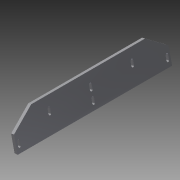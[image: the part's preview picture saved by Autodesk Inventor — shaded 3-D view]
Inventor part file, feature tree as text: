
AUTODESK INVENTOR PART (.ipt)
format: ipt  version: 2011 SP2 (Build 150309200, 309)  size: 1,105,920 bytes
history: native  units: mm
features: extrude x40, sketch x23, projected_geometry x14, fillet x12, mirror x2, pattern_linear x2, plane x1, chamfer x1, hole x1
ambient origin geometry x8: Origin, YZ Plane, XZ Plane, XY Plane, X Axis, Y Axis, Z Axis, Center Point
feature tree (96):
  sketch  "Sketch1"  dims[d0=200.0mm d1=200.0mm]
  extrude  "Extrusion3"  Depth=200.0mm
  extrude  "Extrusion4"  Depth=10.5mm
  extrude  "Extrusion5"  Depth=6.5mm
  extrude  "Extrusion6"  Depth=53.3mm
  extrude  "Extrusion7"  Depth=26.65mm
  sketch  "Sketch4"  dims[d6=6.5mm d8=53.3mm]
  extrude  "Extrusion8"  Depth=5.0mm
  extrude  "Extrusion9"  Depth=5.0mm
  extrude  "Extrusion10"  Depth=4.4mm
  plane  "Work Plane1"
  mirror  "Mirror1"
  sketch  "Sketch9"  dims[d9=53.3mm d10=26.65mm]
  sketch  "Sketch10"  dims[d11=26.65mm d13=5.0mm]
  extrude  "Extrusion16"  Depth=8.0mm
  extrude  "Extrusion17"  Depth=8.0mm
  extrude  "Extrusion18"  Depth=60.0mm
  extrude  "Extrusion19"  Depth=39.0mm
  extrude  "Extrusion20"  Depth=3.65mm
  extrude  "Extrusion21"  Depth=1.5mm
  extrude  "Extrusion22"  Depth=6.6mm
  sketch  "Sketch13"  dims[d18=4.4mm d19=8.0mm]
  extrude  "Extrusion26"  Depth=6.6mm
  extrude  "Extrusion27"  Depth=3.5mm
  extrude  "Extrusion30"  Depth=5.0mm
  extrude  "Extrusion32"  Depth=46.7mm
  extrude  "Extrusion33"  Depth=11.0mm TaperAngle=0.0deg
  extrude  "Extrusion34"  Depth=13.0mm
  chamfer  "Chamfer2"  Distance=7.0mm
  fillet  "Fillet1"  Radius=3.0mm
  extrude  "Extrusion35"  Depth=15.5mm
  extrude  "Extrusion36"  Depth=60.0mm TaperAngle=360.0deg
  sketch  "Sketch21"  dims[d28=1.6mm d29=3.65mm d30=3.65mm]
  extrude  "Extrusion37"  Depth=55.0mm TaperAngle=0.0deg
  extrude  "Extrusion39"  Depth=2.0mm
  extrude  "Extrusion40"  Depth=2.0mm
  fillet  "Fillet2"  Radius=3.65mm
  sketch  "Sketch28"  dims[d44=60.0mm d45=6.6mm]
  extrude  "Extrusion48"  Depth=3.65mm
  extrude  "Extrusion49"  Depth=55.0mm TaperAngle=0.0deg
  extrude  "Extrusion42"  Depth=36.8mm
  extrude  "Extrusion44"  Depth=36.0mm
  fillet  "Fillet4"  Radius=40.0mm
  mirror  "Mirror3"
  fillet  "Fillet3"  Radius=40.0mm
  extrude  "Extrusion45"  Depth=23.0mm TaperAngle=0.0deg
  sketch  "Sketch30"  dims[d49=12.061mm d50=5.0mm]
  extrude  "Extrusion46"  Depth=23.35mm
  extrude  "Extrusion47"  Depth=6.15mm
  hole  "Hole1"  [1 undecoded]
  fillet  "Fillet5"  Radius=2.8mm
  fillet  "Fillet6"  Radius=2.8mm
  fillet  "Fillet7"  Radius=2.8mm
  fillet  "Fillet8"  Radius=32.757mm
  fillet  "Fillet9"  Radius=32.757mm
  fillet  "Fillet10"  Radius=80.957mm
  fillet  "Fillet11"  Radius=80.957mm
  fillet  "Fillet12"  Radius=27.264mm
  extrude  "Extrusion50"  Depth=20.564mm
  extrude  "Extrusion51"  Depth=34.936mm
  sketch  "Sketch34"  dims[d65=38.0mm]
  extrude  "Extrusion53"  Depth=35.936mm
  extrude  "Extrusion54"  Depth=2.0mm
  pattern_linear  "Rectangular Pattern1"  Spacing1=11.0mm  [1 undecoded]
  extrude  "Extrusion57"  Depth=11.0mm
  extrude  "Extrusion58"  Depth=2.0mm
  pattern_linear  "Rectangular Pattern3"  Spacing1=11.0mm  [1 undecoded]
  extrude  "Extrusion59"  Depth=11.0mm
  sketch  "Sketch2"  dims[d2=10.5mm d3=10.5mm]
  sketch  "Sketch3"  dims[d4=57.861mm d5=6.5mm]
  projected_geometry  "Projected Loop1"
  projected_geometry  "Projected Loop7"
  sketch  "Sketch11"  dims[d14=5.0mm d15=5.0mm]
  sketch  "Sketch12"  dims[d16=6.15mm d17=4.4mm]
  projected_geometry  "Projected Loop8"
  sketch  "Sketch15"  dims[d20=5.0mm d21=8.0mm]
  projected_geometry  "Projected Loop9"
  sketch  "Sketch18"  dims[d22=5.0mm d23=60.0mm]
  projected_geometry  "Projected Loop11"
  sketch  "Sketch20"  dims[d25=138.0mm d27=39.0mm]
  projected_geometry  "Projected Loop12"
  sketch  "Sketch25"  dims[d31=3.0mm d32=0.5mm d34=1.5mm d36=5.0mm]
  sketch  "Sketch27"  dims[d37=3.0mm d38=5.0mm d39=8.15mm d41=6.6mm d42=1.5mm d43=0.5mm]
  projected_geometry  "Projected Loop16"
  sketch  "Sketch29"  dims[d47=11.6mm d48=3.5mm]
  sketch  "Sketch31"  dims[d56=8.15mm d57=46.7mm]
  projected_geometry  "Projected Loop17"
  projected_geometry  "Projected Loop18"
  projected_geometry  "Projected Loop19"
  projected_geometry  "Projected Loop20"
  projected_geometry  "Projected Loop21"
  projected_geometry  "Projected Loop22"
  projected_geometry  "Projected Loop23"
  sketch  "Sketch32"  dims[d58=4.0mm d59=0.0mm d60=11.0mm d61=0.0mm]
  sketch  "Sketch33"  dims[d62=55.0mm d63=0.0mm d64=13.0mm]
  sketch  "Sketch35"  dims[d66=36.8mm d67=7.0mm d68=3.0mm d69=15.5mm d70=60.0mm d72=360.0deg d74=55.0mm d75=0.0mm d76=2.0mm d77=2.0mm d78=3.65mm d79=3.65mm d80=55.0mm d81=0.0mm d82=36.8mm d83=36.0mm d84=40.0mm d85=0.0mm d86=40.0mm d87=0.0mm d88=23.0mm d89=0.0mm d90=23.35mm d91=6.15mm d119=2.8mm d120=2.8mm d121=2.8mm d122=2.8mm d135=32.757mm d136=32.757mm d137=80.957mm d138=80.957mm d139=27.264mm d140=20.564mm d141=34.936mm d142=35.936mm d143=2.0mm d144=11.0mm d145=11.0mm d146=2.0mm d147=11.0mm d148=11.0mm d149=2.0mm d150=2.0mm d155=6.0mm d156=6.0mm d157=6.0mm d158=6.0mm d159=3.0mm d160=3.0mm d161=3.0mm d162=3.0mm d163=6.0mm d164=6.0mm d165=3.0mm d166=3.0mm d167=6.0mm d168=6.0mm d169=3.0mm d170=3.0mm d181=3.0mm d182=3.5mm d184=0.0mm d185=0.0mm d186=200.0mm d187=0.0mm d188=200.0mm d189=0.0mm d190=58.0mm d191=0.0mm d192=18.0mm d193=0.0mm d194=40.0mm d195=0.0mm d196=1.570796mm d197=1.570796mm d198=220.0mm d199=220.0mm d200=10.0mm d201=10.0mm d202=5.0mm d203=7.0mm d204=0.0mm d205=0.0mm d215=32.1mm d231=5.0mm d233=12.0mm d234=0.0mm d239=20.0mm d240=0.0mm d256=6.0mm d257=167.0mm d258=6.2mm d259=6.0mm d260=0.0mm d262=22.75mm d266=10.0mm d267=38.9mm d268=5.5mm d269=32.1mm d272=10.0mm d273=12.2mm d276=12.0mm d277=0.0mm d278=28.5mm d279=10.3mm d280=0.0mm d281=5.0mm d282=0.0mm d283=0.5mm d284=5.3mm d285=45.0deg d286=1.0mm d287=5.0mm d288=0.0mm d289=3.0mm d290=3.0mm d291=10.0mm d292=0.0mm d293=6.15mm d294=4.4mm d295=2.0mm d296=3.0mm d297=10.0mm d298=0.0mm d306=41.0mm d307=0.0mm d308=6.0mm d309=6.0mm d310=2.575mm d311=2.575mm d312=2.0mm d313=2.0mm d315=8.956377mm d316=161.0mm d317=10.0mm d318=7.0mm d319=0.0mm d320=32.5mm d335=32.5mm d336=7.0mm d337=12.0mm d338=9.25mm d339=-0.872665mm d343=1.0mm d344=9.25mm d345=-0.872665mm d346=8.0mm d347=4.0mm d348=10.0mm d349=20.0mm d350=0.0mm d351=179.0mm d352=0.0mm d353=179.0mm d354=0.0mm d355=1.5mm d356=3.5mm d357=3.5mm d358=89.5mm d359=89.5mm d360=5.0mm d361=17.5mm d362=2.0mm d363=6.0mm d364=3.0mm d365=2.0mm d366=90.0deg d367=2.0mm d368=3.665191mm d369=6.0mm d370=6.0mm d371=6.0mm d372=6.0mm d373=6.0mm d376=6.0mm d377=2.0mm d378=2.0mm d379=2.0mm d380=3.0mm d382=3.0mm d383=3.0mm d384=3.0mm d386=55.0mm d387=0.0mm d388=40.0mm d389=0.0mm d390=26.0mm d391=69.0mm d392=48.0mm d393=3.0mm d394=13.0mm d395=13.0mm d396=3.0mm d397=1.0mm d398=0.5mm d399=0.5mm d400=1.0mm d401=0.5mm d402=1.0mm d403=15.0mm d404=1.0mm d405=10.0mm d406=0.0mm d407=10.0mm d408=0.0mm d409=3.0mm d410=3.0mm d411=2.0mm d412=2.0mm d416=3.0mm d431=4.0mm d432=0.0mm d433=0.5mm d434=-7.853982mm d439=30.0mm d441=86.0mm d445=3.0mm d446=3.0mm d447=2.0mm d448=2.0mm d449=2.5mm d450=2.5mm d451=0.5mm d452=0.0mm d453=0.5mm d454=-7.853982mm d455=30.0mm d457=48.029mm d458=0.0mm d459=10.0mm d460=0.0mm]
note: 3 required parameter values undecoded (feature->parameter linkage not recoverable at this tier; creation-order binding heuristic only, values carry confidence <= 0.55)
